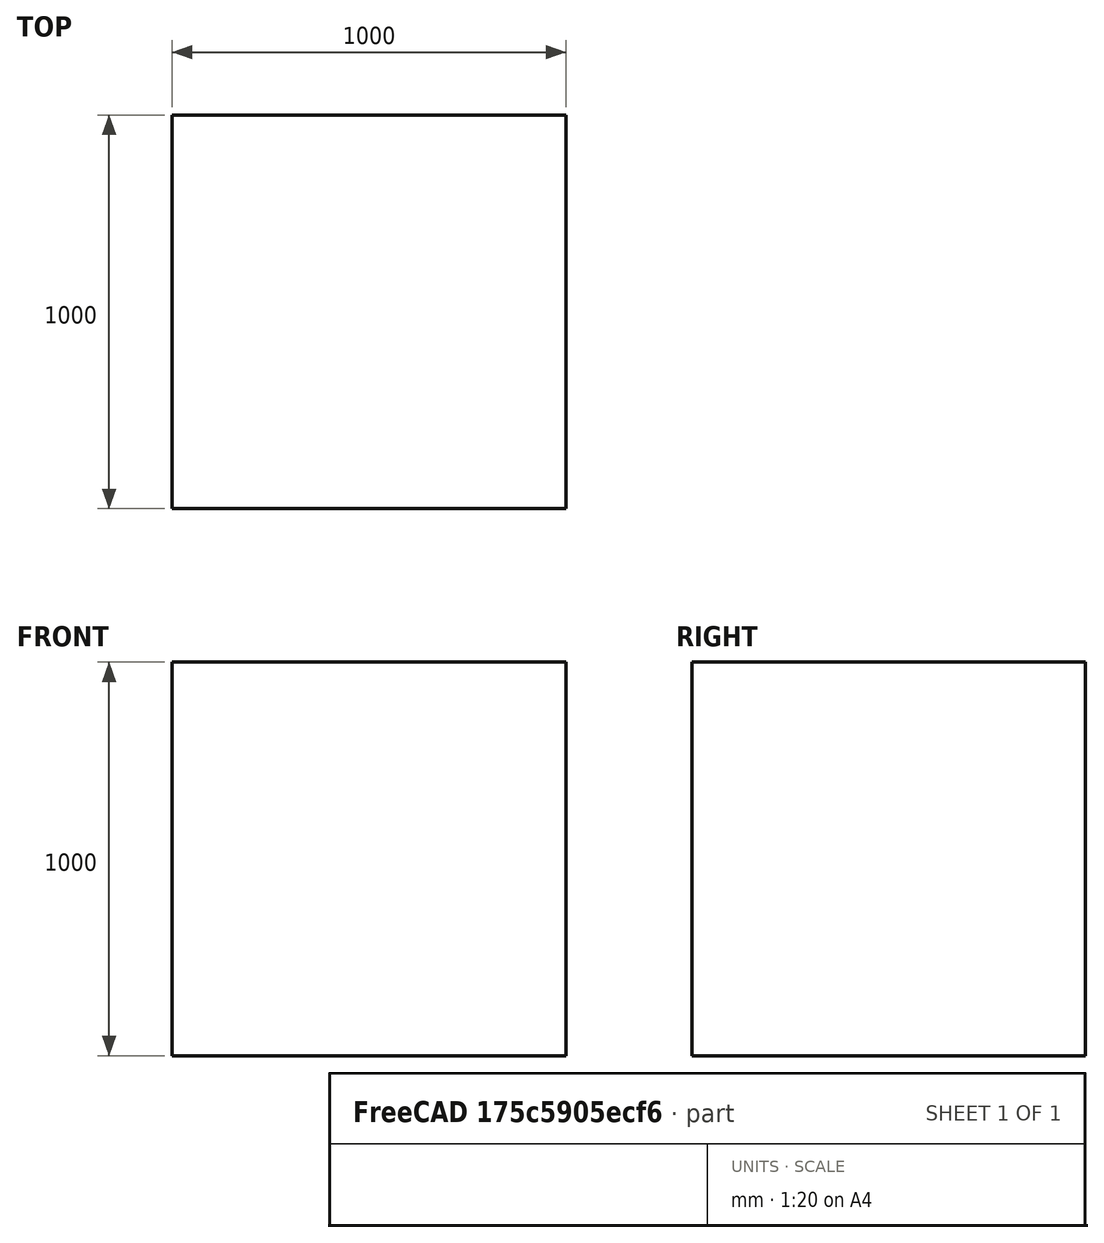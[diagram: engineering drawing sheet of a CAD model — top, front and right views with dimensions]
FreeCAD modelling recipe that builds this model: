
FCSTD DOCUMENT  (FreeCAD 0.19R)
Label: test_box
License: All rights reserved
LicenseURL: http://en.wikipedia.org/wiki/All_rights_reserved
objects: Sketcher::SketchObject×1, PartDesign::Pad×1, PartDesign::Body×1
note: 4 computed .brp shape members not serialized (recipe doc carries the construction recipe); baked Part::Feature solids carry a one-line shape summary decoded from their .brp

FEATURE [Sketcher::SketchObject] Sketch
  FullyConstrained = true
  MapMode = 5
  Support = -> [XY_Plane]
  sketch-geometry (4):
    g0: LineSegment StartX=500 StartY=500 StartZ=0 EndX=-500 EndY=500 EndZ=0
    g1: LineSegment StartX=-500 StartY=500 StartZ=0 EndX=-500 EndY=-500 EndZ=0
    g2: LineSegment StartX=-500 StartY=-500 StartZ=0 EndX=500 EndY=-500 EndZ=0
    g3: LineSegment StartX=500 StartY=-500 StartZ=0 EndX=500 EndY=500 EndZ=0
  constraints (11):
    c: Coincident(g0,g1)
    c: Coincident(g1,g2)
    c: Coincident(g2,g3)
    c: Coincident(g3,g0)
    c: Horizontal(g0)
    c: Horizontal(g2)
    c: Vertical(g1)
    c: Vertical(g3)
    c: Symmetric(g0,g1,g-1)
    c: DistanceX(g0,g0) = 1000
    c: DistanceY(g3,g3) = 1000
FEATURE [PartDesign::Pad] Pad
  Direction = (1,1,1)
  Length = 1000
  Length2 = 100
  Midplane = true
  Profile = -> Sketch
  Type = 0
FEATURE [PartDesign::Body] Body
  Group = -> [Sketch,Pad]
  Origin = -> Origin
  Tip = -> Pad
